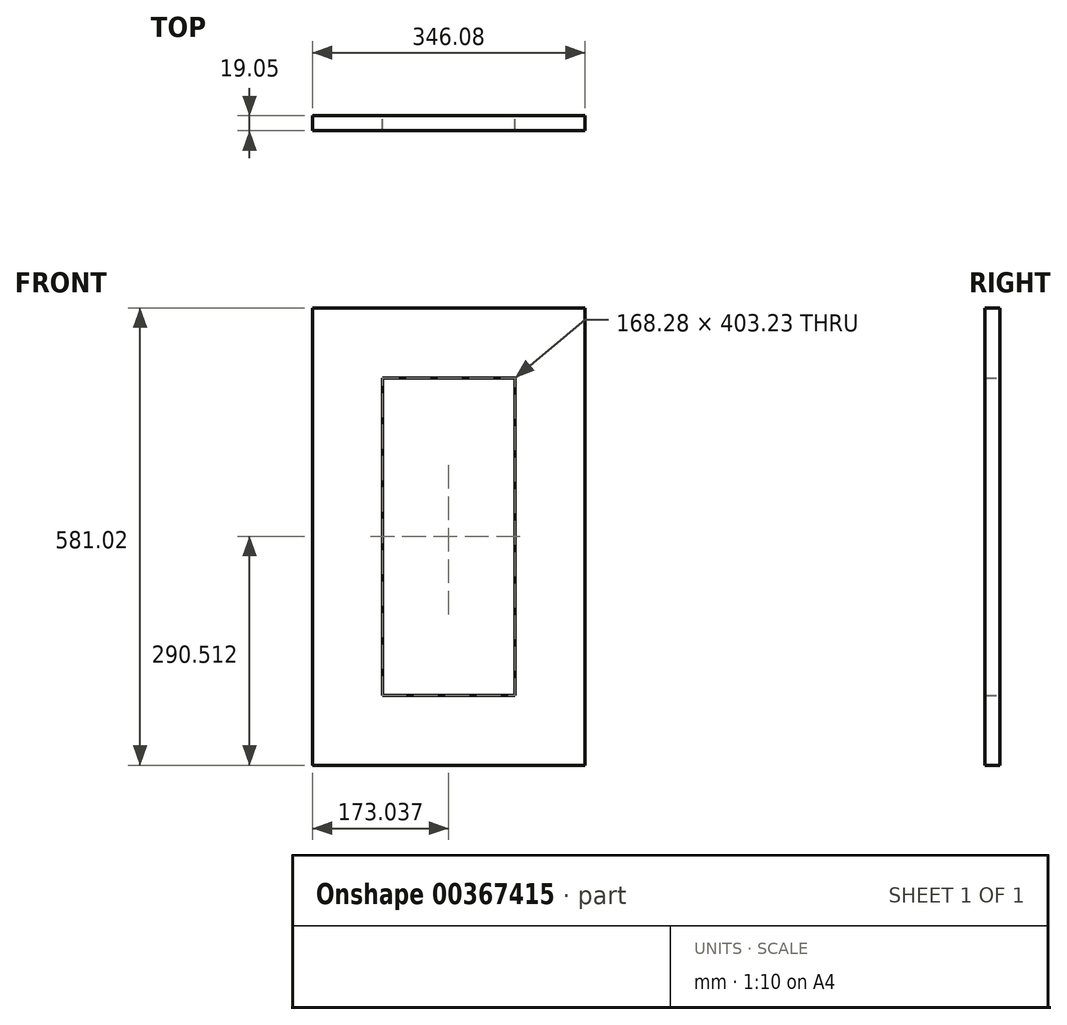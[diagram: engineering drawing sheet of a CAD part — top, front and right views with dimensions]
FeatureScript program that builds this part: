
annotation { "Feature Type Name" : "Feature", "Feature Type Description" : "" }
export const myFeature = defineFeature(function(context is Context, id is Id, definition is map)
    precondition{}
    {
        {
            var Q0;
            Q0=qCreatedBy(makeId("Front.planeOp"),FACE);
            var sketch = newSketch(context, id + "F0", { "sketchPlane" : qUnion([Q0])});
            skLineSegment(sketch, "E0.left", {"start": v(0, 0) * mm, "end": v(0, 581.02) * mm});
            skLineSegment(sketch, "E0.right", {"start": v(88.9, 88.9) * mm, "end": v(88.9, 492.13) * mm});
            skLineSegment(sketch, "E1.left", {"start": v(257.18, 88.9) * mm, "end": v(257.18, 492.13) * mm});
            skLineSegment(sketch, "E1.right", {"start": v(346.08, 0) * mm, "end": v(346.08, 581.02) * mm});
            skLineSegment(sketch, "E2", {"start": v(257.18, 492.13) * mm, "end": v(88.9, 492.13) * mm});
            skLineSegment(sketch, "E3", {"start": v(346.08, 581.02) * mm, "end": v(0, 581.02) * mm});
            skLineSegment(sketch, "E4", {"start": v(257.18, 88.9) * mm, "end": v(88.9, 88.9) * mm});
            skLineSegment(sketch, "E5", {"start": v(346.08, 0) * mm, "end": v(0, 0) * mm});
            skSolve(sketch);
        }
        {
            var Q0;
            Q0 = qSketchRegion(id + "F0", true);
            extrude(context, id + "F1", {"entities" : qUnion([Q0]), "depth" : 19.05 * mm});
        }
    });
